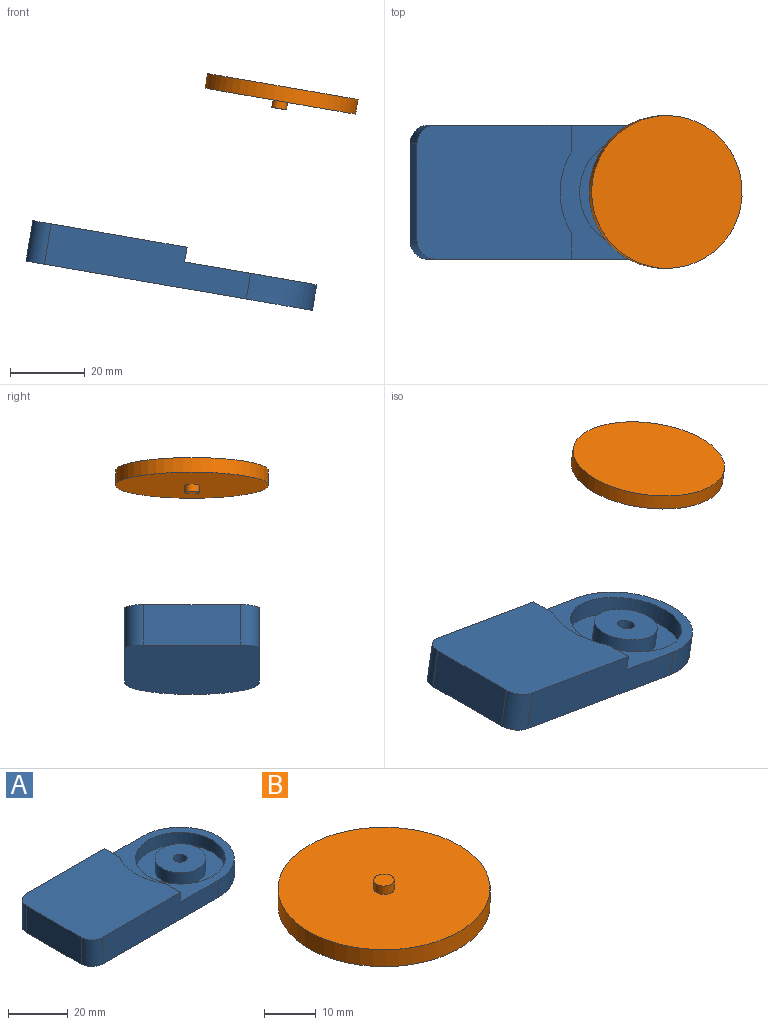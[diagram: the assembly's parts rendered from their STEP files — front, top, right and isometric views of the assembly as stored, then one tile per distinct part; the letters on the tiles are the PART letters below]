
ASSEMBLY  parts=2 mates=1
PART A: 18 faces, bbox 78x36x11 mm
  f0: cylinder r=18mm len=36mm, axis (0,0,1), area 395.8mm2, adj f1,f3,f4,f6
  f1: plane 55x11mm, normal (0,1,0), area 533mm2, adj f0,f4,f6,f12,f15,f16
  f2: plane 26x11mm, normal (-1,0,0), area 286mm2, adj f4,f15,f16,f17
  f3: plane 55x11mm, normal (0,-1,0), area 533mm2, adj f0,f4,f6,f13,f15,f17
  f4: plane 78x36mm, normal (0,0,-1), area 2658.2mm2, adj f0,f1,f2,f3,f16,f17
  f5: cylinder r=15mm len=30mm, axis (0,0,-1), area 471.2mm2, adj f6,f7
  f6: plane 39x36mm, normal (0,0,1), area 494mm2, adj f0,f1,f3,f5,f12,f13,f14
  f7: plane 30x30mm, normal (0,0,1), area 479.9mm2, adj f5,f9
  f8: cylinder r=2.25mm len=5mm, axis (0,0,-1), area 70.7mm2, adj f10,f11
  f9: cylinder r=8.5mm len=17mm, axis (0,0,-1), area 267mm2, adj f7,f10
  f10: plane 17x17mm, normal (0,0,1), area 211.1mm2, adj f8,f9
  f11: plane 4.5x4.5mm, normal (0,0,1), area 15.9mm2, adj f8
  f12: plane 7.18x4mm, normal (1,0,0), area 28.7mm2, adj f1,f6,f14,f15
  f13: plane 7.18x4mm, normal (1,0,0), area 28.7mm2, adj f3,f6,f14,f15
  f14: cylinder r=21mm len=21.63mm, axis (0,0,-1), area 90.9mm2, adj f6,f12,f13,f15
  f15: plane 42x36mm, normal (0,0,1), area 1457.3mm2, adj f1,f2,f3,f12,f13,f14,f16,f17
  f16: cylinder r=5mm len=11mm, axis (0,0,-1), area 86.4mm2, adj f1,f2,f4,f15
  f17: cylinder r=5mm len=11mm, axis (0,0,1), area 86.4mm2, adj f2,f3,f4,f15
PART B: 5 faces, bbox 41x41x6 mm
  f0: cylinder r=20.5mm len=41mm, axis (0,0,1), area 515.2mm2, adj f1,f2
  f1: plane 41x41mm, normal (0,0,-1), area 1320.3mm2, adj f0
  f2: plane 41x41mm, normal (0,0,1), area 1307.7mm2, adj f0,f3
  f3: cylinder r=2mm len=4mm, axis (0,0,-1), area 25.1mm2, adj f2,f4
  f4: plane 4x4mm, normal (0,0,1), area 12.6mm2, adj f3
PLACE A rot(axis=(0,1,0),9.8deg) t=(-43.91,11.4,-5.17)mm
PLACE B rot(axis=(0,-1,0),170.2deg) t=(-35.09,11.4,45.96)mm
MATE slider B.f3 <-> A.f8  axis (-0.17,0,-0.99) through (-35.43,11.4,43.99)mm
